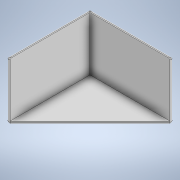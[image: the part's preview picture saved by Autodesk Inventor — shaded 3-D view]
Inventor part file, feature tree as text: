
AUTODESK INVENTOR PART (.ipt)
format: ipt  version: 2021 (Build 250183000, 183)  size: 142,848 bytes
history: native  units: mm
features: fillet x3, extrude x2, sketch x2
ambient origin geometry x8: Origin, YZ Plane, XZ Plane, XY Plane, X Axis, Y Axis, Z Axis, Center Point
bodies: Solid1 (feature_tree)
feature tree (7):
  extrude  "Extrusion1"  Depth=15.0mm
  extrude  "Extrusion2"  Depth=0.5mm TaperAngle=0.0deg
  fillet  "Fillet1"  Radius=40.0mm
  fillet  "Fillet2"  [1 undecoded]
  fillet  "Fillet3"  Radius=1.5mm
  sketch  "Sketch1"  dims[d0=40.0mm d2=15.0mm]
  sketch  "Sketch2"  dims[d3=45.0deg d4=26.5mm d5=0.0mm d6=40.0mm d8=0.0mm d9=1.5mm d10=1.5mm d11=25.0mm d12=0.0mm d13=1.0mm d14=1.0mm d15=0.5mm]
note: 1 required parameter value undecoded (feature->parameter linkage not recoverable at this tier; creation-order binding heuristic only, values carry confidence <= 0.55)
